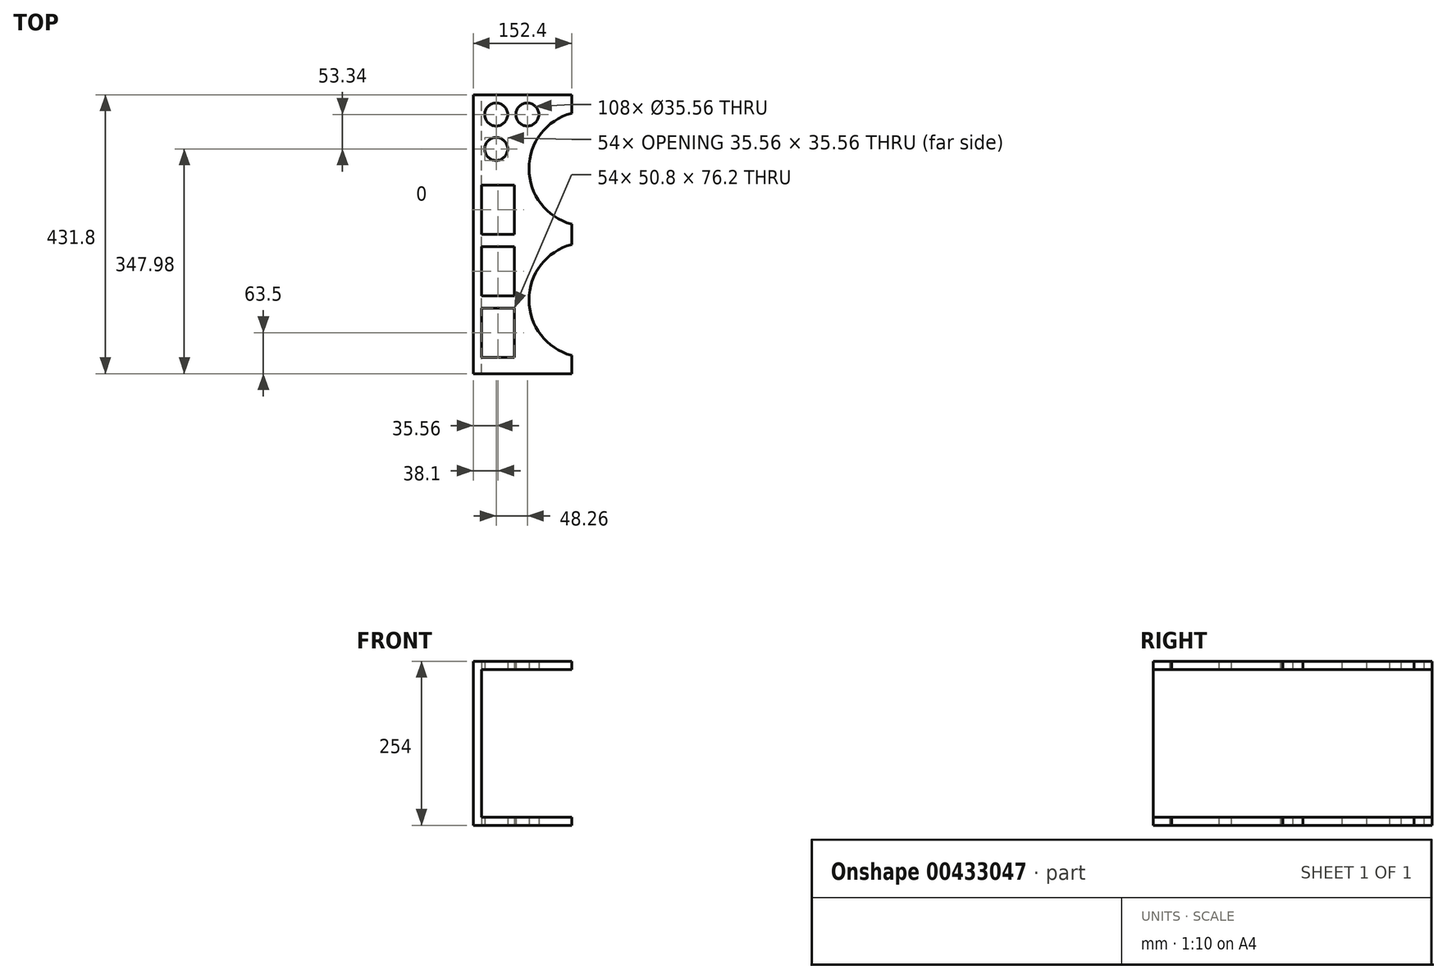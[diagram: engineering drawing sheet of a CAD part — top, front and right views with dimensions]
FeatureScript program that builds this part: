
annotation { "Feature Type Name" : "Feature", "Feature Type Description" : "" }
export const myFeature = defineFeature(function(context is Context, id is Id, definition is map)
    precondition{}
    {
        {
            var Q0;
            Q0=qCreatedBy(makeId("Front.planeOp"),FACE);
            var sketch = newSketch(context, id + "F0", { "sketchPlane" : qUnion([Q0])});
            skLineSegment(sketch, "E0", {"start": v(0, 0) * mm, "end": v(152.4, 0) * mm});
            skLineSegment(sketch, "E1", {"start": v(152.4, 0) * mm, "end": v(152.4, 12.7) * mm});
            skLineSegment(sketch, "E2", {"start": v(152.4, 12.7) * mm, "end": v(12.7, 12.7) * mm});
            skLineSegment(sketch, "E3", {"start": v(12.7, 12.7) * mm, "end": v(12.7, 241.3) * mm});
            skLineSegment(sketch, "E4", {"start": v(12.7, 241.3) * mm, "end": v(152.4, 241.3) * mm});
            skLineSegment(sketch, "E5", {"start": v(152.4, 241.3) * mm, "end": v(152.4, 254) * mm});
            skLineSegment(sketch, "E6", {"start": v(152.4, 254) * mm, "end": v(0, 254) * mm});
            skLineSegment(sketch, "E7", {"start": v(0, 254) * mm, "end": v(0, 0) * mm});
            skSolve(sketch);
        }
        {
            var Q0;
            Q0=makeQuery(id+"F0.imprint","IMPRINT",FACE,{"disambiguationData":[TD([[makeQuery(id+"F0.imprint","IMPRINT",EDGE,{"derivedFrom":sQuery(id+"F0.wireOp",EDGE,"E0")}),1.0]])]});
            extrude(context, id + "F1", {"entities" : qUnion([Q0]), "depth" : 431.8 * mm});
        }
        {
            var Q0;
            Q0=qCreatedBy(makeId("Top.planeOp"),FACE);
            var sketch = newSketch(context, id + "F2", { "sketchPlane" : qUnion([Q0])});
            skLineSegment(sketch, "E8", {"start": v(152.4, -28.39) * mm, "end": v(152.4, -200.21) * mm});
            skLineSegment(sketch, "E9", {"start": v(152.4, -231.59) * mm, "end": v(152.4, -403.41) * mm});
            skArc(sketch, "E10", {"start": v(152.4, -231.59) * mm, "mid": v(86.36, -317.5) * mm, "end": v(152.4, -403.41) * mm});
            skArc(sketch, "E11", {"start": v(152.4, -28.39) * mm, "mid": v(86.36, -114.3) * mm, "end": v(152.4, -200.21) * mm});
            skLineSegment(sketch, "E12.bottom", {"start": v(12.7, -406.4) * mm, "end": v(63.5, -406.4) * mm});
            skLineSegment(sketch, "E12.top", {"start": v(12.7, -330.2) * mm, "end": v(63.5, -330.2) * mm});
            skLineSegment(sketch, "E12.left", {"start": v(12.7, -406.4) * mm, "end": v(12.7, -330.2) * mm});
            skLineSegment(sketch, "E12.right", {"start": v(63.5, -406.4) * mm, "end": v(63.5, -330.2) * mm});
            skLineSegment(sketch, "E13.bottom", {"start": v(12.7, -311.15) * mm, "end": v(63.5, -311.15) * mm});
            skLineSegment(sketch, "E13.top", {"start": v(12.7, -234.95) * mm, "end": v(63.5, -234.95) * mm});
            skLineSegment(sketch, "E13.left", {"start": v(12.7, -311.15) * mm, "end": v(12.7, -234.95) * mm});
            skLineSegment(sketch, "E13.right", {"start": v(63.5, -311.15) * mm, "end": v(63.5, -234.95) * mm});
            skLineSegment(sketch, "E14.bottom", {"start": v(12.7, -215.9) * mm, "end": v(63.5, -215.9) * mm});
            skLineSegment(sketch, "E14.top", {"start": v(12.7, -139.7) * mm, "end": v(63.5, -139.7) * mm});
            skLineSegment(sketch, "E14.left", {"start": v(12.7, -215.9) * mm, "end": v(12.7, -139.7) * mm});
            skLineSegment(sketch, "E14.right", {"start": v(63.5, -215.9) * mm, "end": v(63.5, -139.7) * mm});
            skCircle(sketch, "E15", {"center": v(35.56, -83.82) * mm, "radius": 17.78 * mm});
            skCircle(sketch, "E16", {"center": v(35.56, -30.48) * mm, "radius": 17.78 * mm});
            skCircle(sketch, "E17", {"center": v(83.82, -30.48) * mm, "radius": 17.78 * mm});
            skSolve(sketch);
        }
        {
            var Q0;
            Q0=makeQuery(id+"F2.imprint","IMPRINT",FACE,{"disambiguationData":[TD([[makeQuery(id+"F2.imprint","IMPRINT",EDGE,{"derivedFrom":sQuery(id+"F2.wireOp",EDGE,"E9")}),-1.0]])]});
            var Q1;
            Q1=makeQuery(id+"F2.imprint","IMPRINT",FACE,{"disambiguationData":[TD([[makeQuery(id+"F2.imprint","IMPRINT",EDGE,{"derivedFrom":sQuery(id+"F2.wireOp",EDGE,"E8")}),-1.0]])]});
            var Q2;
            Q2=makeQuery(id+"F2.imprint","IMPRINT",FACE,{"disambiguationData":[TD([[makeQuery(id+"F2.imprint","IMPRINT",EDGE,{"derivedFrom":sQuery(id+"F2.wireOp",EDGE,"E12.bottom")}),1.0]])]});
            var Q3;
            Q3=makeQuery(id+"F2.imprint","IMPRINT",FACE,{"disambiguationData":[TD([[makeQuery(id+"F2.imprint","IMPRINT",EDGE,{"derivedFrom":sQuery(id+"F2.wireOp",EDGE,"E13.bottom")}),1.0]])]});
            var Q4;
            Q4=makeQuery(id+"F2.imprint","IMPRINT",FACE,{"disambiguationData":[TD([[makeQuery(id+"F2.imprint","IMPRINT",EDGE,{"derivedFrom":sQuery(id+"F2.wireOp",EDGE,"E14.bottom")}),1.0]])]});
            var Q5;
            Q5=makeQuery(id+"F2.imprint","IMPRINT",FACE,{"disambiguationData":[TD([[makeQuery(id+"F2.imprint","IMPRINT",EDGE,{"derivedFrom":sQuery(id+"F2.wireOp",EDGE,"E15")}),1.0]])]});
            var Q6;
            Q6=makeQuery(id+"F2.imprint","IMPRINT",FACE,{"disambiguationData":[TD([[makeQuery(id+"F2.imprint","IMPRINT",EDGE,{"derivedFrom":sQuery(id+"F2.wireOp",EDGE,"E16")}),1.0]])]});
            var Q7;
            Q7=makeQuery(id+"F2.imprint","IMPRINT",FACE,{"disambiguationData":[TD([[makeQuery(id+"F2.imprint","IMPRINT",EDGE,{"derivedFrom":sQuery(id+"F2.wireOp",EDGE,"E17")}),1.0]])]});
            extrude(context, id + "F3", {"entities" : qUnion([Q0, Q1, Q2, Q3, Q4, Q5, Q6, Q7]), "operationType" : NewBodyOperationType.REMOVE, "endBound" : BoundingType.THROUGH_ALL, "depth" : 25.4 * mm});
        }
    });
